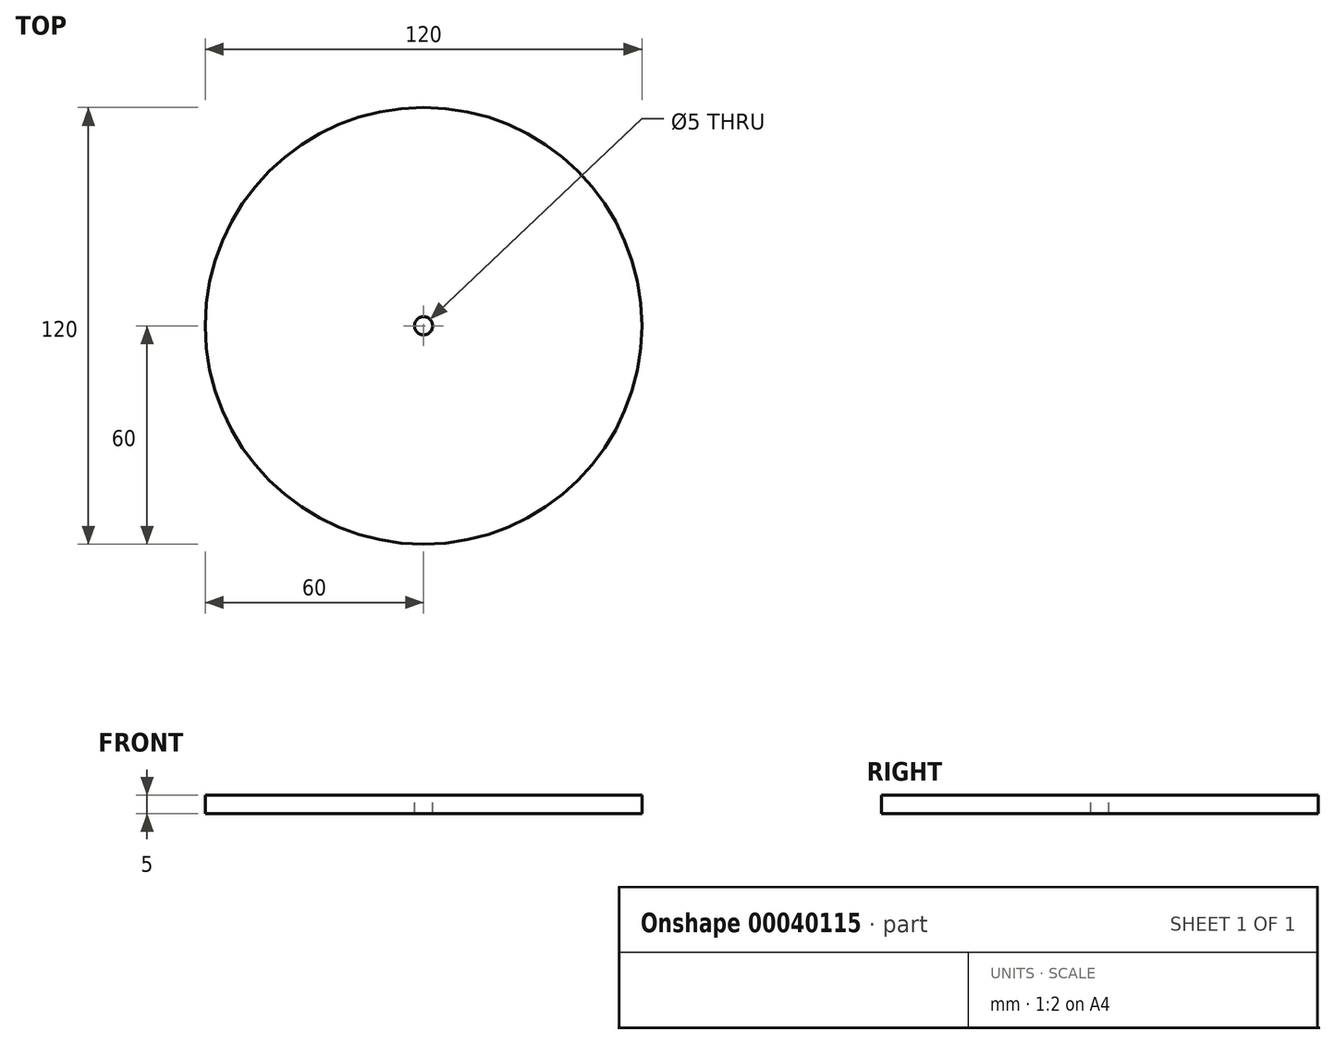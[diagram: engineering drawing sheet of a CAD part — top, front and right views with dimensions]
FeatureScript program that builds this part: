
annotation { "Feature Type Name" : "Feature", "Feature Type Description" : "" }
export const myFeature = defineFeature(function(context is Context, id is Id, definition is map)
    precondition{}
    {
        {
            var Q0;
            Q0=qCreatedBy(makeId("Top.planeOp"),FACE);
            var sketch = newSketch(context, id + "F0", { "sketchPlane" : qUnion([Q0])});
            skCircle(sketch, "E0", {"center": v(0, 0) * mm, "radius": 60 * mm});
            skSolve(sketch);
        }
        {
            var Q0;
            Q0=makeQuery(id+"F0.imprint","IMPRINT",FACE,{"disambiguationData":[TD([[makeQuery(id+"F0.imprint","IMPRINT",EDGE,{"derivedFrom":sQuery(id+"F0.wireOp",EDGE,"E0")}),1.0]])]});
            extrude(context, id + "F1", {"entities" : qUnion([Q0]), "depth" : 5 * mm});
        }
        {
            var Q0;
            Q0=makeQuery(id+"F1.opExtrude","CAP_FACE",FACE,{"disambiguationData":[OSD([sQuery(id+"F0.wireOp",EDGE,"E0")])],"isStart":false});
            var sketch = newSketch(context, id + "F2", { "sketchPlane" : qUnion([Q0])});
            skCircle(sketch, "E1", {"center": v(0, 0) * mm, "radius": 2.5 * mm});
            skSolve(sketch);
        }
        {
            var Q0;
            Q0=sQuery(id+"F2.wireOp",VERTEX,"E1.center");
            var Q1;
            Q1=makeQuery(id+"F1.opExtrude","SWEPT_BODY",BODY,{"disambiguationData":[OSD([sQuery(id+"F0.wireOp",EDGE,"E0")])]});
            hole(context, id + "F3", {"style" : HoleStyle.SIMPLE, "holeDiameter" : 5 * mm, "endStyle" : HoleEndStyle.THROUGH, "locations" : qUnion([Q0]), "scope" : qUnion([Q1])});
        }
    });
